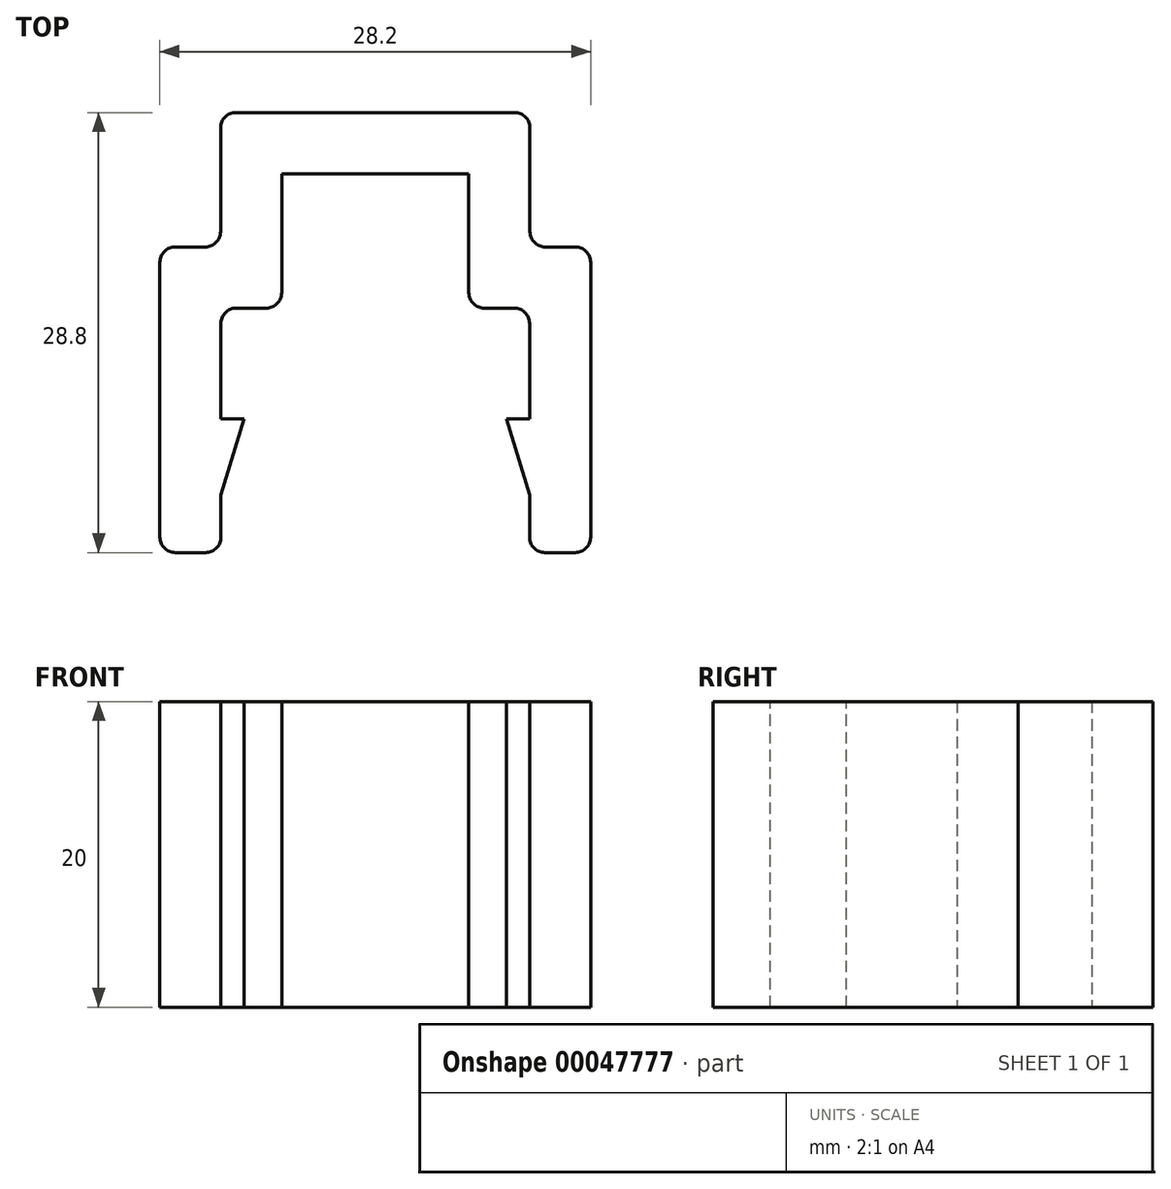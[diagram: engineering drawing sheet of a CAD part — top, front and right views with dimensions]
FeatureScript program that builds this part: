
annotation { "Feature Type Name" : "Feature", "Feature Type Description" : "" }
export const myFeature = defineFeature(function(context is Context, id is Id, definition is map)
    precondition{}
    {
        {
            var Q0;
            Q0=qCreatedBy(makeId("Top.planeOp"),FACE);
            var sketch = newSketch(context, id + "F3", { "sketchPlane" : qUnion([Q0])});
            skLineSegment(sketch, "E0", {"start": v(0, 0) * mm, "end": v(0, 20) * mm});
            skLineSegment(sketch, "E1", {"start": v(0, 20) * mm, "end": v(0, 20) * mm});
            skLineSegment(sketch, "E2", {"start": v(0, 20) * mm, "end": v(3.97, 20) * mm});
            skLineSegment(sketch, "E3", {"start": v(3.97, 20) * mm, "end": v(3.97, 20) * mm});
            skLineSegment(sketch, "E4", {"start": v(3.97, 20) * mm, "end": v(3.97, 28.8) * mm});
            skLineSegment(sketch, "E5", {"start": v(3.97, 28.8) * mm, "end": v(3.97, 28.8) * mm});
            skLineSegment(sketch, "E6", {"start": v(3.97, 28.8) * mm, "end": v(24.23, 28.8) * mm});
            skLineSegment(sketch, "E7", {"start": v(24.23, 28.8) * mm, "end": v(24.23, 20) * mm});
            skLineSegment(sketch, "E8", {"start": v(24.23, 20) * mm, "end": v(28.2, 20) * mm});
            skLineSegment(sketch, "E9", {"start": v(28.2, 20) * mm, "end": v(28.2, 0) * mm});
            skLineSegment(sketch, "E10.0", {"start": v(24.2, 16) * mm, "end": v(24.2, 0) * mm});
            skLineSegment(sketch, "E10.1", {"start": v(20.23, 16) * mm, "end": v(24.2, 16) * mm});
            skLineSegment(sketch, "E10.2", {"start": v(20.23, 24.8) * mm, "end": v(20.23, 16) * mm});
            skLineSegment(sketch, "E10.3", {"start": v(4, 0) * mm, "end": v(4, 16) * mm});
            skLineSegment(sketch, "E10.4", {"start": v(4, 16) * mm, "end": v(7.97, 16) * mm});
            skLineSegment(sketch, "E10.5", {"start": v(7.97, 16) * mm, "end": v(7.97, 24.8) * mm});
            skLineSegment(sketch, "E10.6", {"start": v(7.97, 24.8) * mm, "end": v(20.23, 24.8) * mm});
            skLineSegment(sketch, "E11", {"start": v(0, 0) * mm, "end": v(4, 0) * mm});
            skLineSegment(sketch, "E12", {"start": v(24.2, 0) * mm, "end": v(28.2, 0) * mm});
            skSolve(sketch);
        }
        {
            var Q0;
            Q0 = qSketchRegion(id + "F3", true);
            extrude(context, id + "F0", {"entities" : qUnion([Q0]), "depth" : 20 * mm});
        }
        {
            var Q0;
            Q0=makeQuery(id+"F0.opExtrude","SWEPT_EDGE",EDGE,{"disambiguationData":[OSD([sQuery(id+"F3.wireOp",EDGE,"E10.3"),sQuery(id+"F3.wireOp",EDGE,"E10.4")])]});
            var Q1;
            Q1=makeQuery(id+"F0.opExtrude","SWEPT_EDGE",EDGE,{"disambiguationData":[OSD([sQuery(id+"F3.wireOp",EDGE,"E10.0"),sQuery(id+"F3.wireOp",EDGE,"E10.1")])]});
            var Q2;
            Q2=makeQuery(id+"F0.opExtrude","SWEPT_EDGE",EDGE,{"disambiguationData":[OSD([sQuery(id+"F3.wireOp",EDGE,"E10.4"),sQuery(id+"F3.wireOp",EDGE,"E10.5")])]});
            var Q3;
            Q3=makeQuery(id+"F0.opExtrude","SWEPT_EDGE",EDGE,{"disambiguationData":[OSD([sQuery(id+"F3.wireOp",EDGE,"E10.1"),sQuery(id+"F3.wireOp",EDGE,"E10.2")])]});
            var Q4;
            Q4=makeQuery(id+"F0.opExtrude","SWEPT_EDGE",EDGE,{"disambiguationData":[OSD([sQuery(id+"F3.wireOp",EDGE,"E0"),sQuery(id+"F3.wireOp",EDGE,"E11")])]});
            var Q5;
            Q5=makeQuery(id+"F0.opExtrude","SWEPT_EDGE",EDGE,{"disambiguationData":[OSD([sQuery(id+"F3.wireOp",EDGE,"E10.3"),sQuery(id+"F3.wireOp",EDGE,"E11")])]});
            var Q6;
            Q6=makeQuery(id+"F0.opExtrude","SWEPT_EDGE",EDGE,{"disambiguationData":[OSD([sQuery(id+"F3.wireOp",EDGE,"E10.0"),sQuery(id+"F3.wireOp",EDGE,"E12")])]});
            var Q7;
            Q7=makeQuery(id+"F0.opExtrude","SWEPT_EDGE",EDGE,{"disambiguationData":[OSD([sQuery(id+"F3.wireOp",EDGE,"E9"),sQuery(id+"F3.wireOp",EDGE,"E12")])]});
            var Q8;
            Q8=makeQuery(id+"F0.opExtrude","SWEPT_EDGE",EDGE,{"disambiguationData":[OSD([sQuery(id+"F3.wireOp",EDGE,"E0"),sQuery(id+"F3.wireOp",EDGE,"E2")])]});
            var Q9;
            Q9=makeQuery(id+"F0.opExtrude","SWEPT_EDGE",EDGE,{"disambiguationData":[OSD([sQuery(id+"F3.wireOp",EDGE,"E4"),sQuery(id+"F3.wireOp",EDGE,"E6")])]});
            var Q10;
            Q10=makeQuery(id+"F0.opExtrude","SWEPT_EDGE",EDGE,{"disambiguationData":[OSD([sQuery(id+"F3.wireOp",EDGE,"E2"),sQuery(id+"F3.wireOp",EDGE,"E4")])]});
            var Q11;
            Q11=makeQuery(id+"F0.opExtrude","SWEPT_EDGE",EDGE,{"disambiguationData":[OSD([sQuery(id+"F3.wireOp",EDGE,"E6"),sQuery(id+"F3.wireOp",EDGE,"E7")])]});
            var Q12;
            Q12=makeQuery(id+"F0.opExtrude","SWEPT_EDGE",EDGE,{"disambiguationData":[OSD([sQuery(id+"F3.wireOp",EDGE,"E7"),sQuery(id+"F3.wireOp",EDGE,"E8")])]});
            var Q13;
            Q13=makeQuery(id+"F0.opExtrude","SWEPT_EDGE",EDGE,{"disambiguationData":[OSD([sQuery(id+"F3.wireOp",EDGE,"E8"),sQuery(id+"F3.wireOp",EDGE,"E9")])]});
            fillet(context, id + "F4", {"entities" : qUnion([Q0, Q1, Q2, Q3, Q4, Q5, Q6, Q7, Q8, Q9, Q10, Q11, Q12, Q13]), "radius" : 1 * mm, "tangentPropagation" : true, "allowEdgeOverflow" : false});
        }
        {
            var Q0;
            Q0=makeQuery(id+"F0.opExtrude","CAP_FACE",FACE,{"disambiguationData":[OSD([sQuery(id+"F3.wireOp",EDGE,"E0"),sQuery(id+"F3.wireOp",EDGE,"E2"),sQuery(id+"F3.wireOp",EDGE,"E4"),sQuery(id+"F3.wireOp",EDGE,"E6"),sQuery(id+"F3.wireOp",EDGE,"E7"),sQuery(id+"F3.wireOp",EDGE,"E8"),sQuery(id+"F3.wireOp",EDGE,"E9"),sQuery(id+"F3.wireOp",EDGE,"E10.0"),sQuery(id+"F3.wireOp",EDGE,"E10.1"),sQuery(id+"F3.wireOp",EDGE,"E10.2"),sQuery(id+"F3.wireOp",EDGE,"E10.3"),sQuery(id+"F3.wireOp",EDGE,"E10.4"),sQuery(id+"F3.wireOp",EDGE,"E10.5"),sQuery(id+"F3.wireOp",EDGE,"E10.6"),sQuery(id+"F3.wireOp",EDGE,"E11"),sQuery(id+"F3.wireOp",EDGE,"E12")])],"isStart":false});
            var sketch = newSketch(context, id + "F1", { "sketchPlane" : qUnion([Q0])});
            skLineSegment(sketch, "E13", {"start": v(4, 8.75) * mm, "end": v(5.5, 8.75) * mm});
            skLineSegment(sketch, "E14", {"start": v(5.5, 8.75) * mm, "end": v(4, 3.75) * mm});
            skLineSegment(sketch, "E15", {"start": v(4, 3.75) * mm, "end": v(4, 8.75) * mm});
            skLineSegment(sketch, "E16", {"start": v(14.1, 24.8) * mm, "end": v(14.1, 0) * mm, "construction": true});
            skLineSegment(sketch, "E17.MirrorCS", {"start": v(22.7, 8.75) * mm, "end": v(24.2, 3.75) * mm});
            skLineSegment(sketch, "E18.MirrorCS", {"start": v(24.2, 3.75) * mm, "end": v(24.2, 8.75) * mm});
            skLineSegment(sketch, "E19.MirrorCS", {"start": v(24.2, 8.75) * mm, "end": v(22.7, 8.75) * mm});
            skSolve(sketch);
        }
        {
            var Q0;
            Q0=makeQuery(id+"F1.imprint","IMPRINT",FACE,{"disambiguationData":[TD([[makeQuery(id+"F1.imprint","IMPRINT",EDGE,{"derivedFrom":sQuery(id+"F1.wireOp",EDGE,"E13")}),-1.0]])]});
            var Q1;
            Q1=makeQuery(id+"F1.imprint","IMPRINT",FACE,{"disambiguationData":[TD([[makeQuery(id+"F1.imprint","IMPRINT",EDGE,{"derivedFrom":sQuery(id+"F1.wireOp",EDGE,"E17.MirrorCS")}),1.0]])]});
            extrude(context, id + "F2", {"entities" : qUnion([Q0, Q1]), "operationType" : NewBodyOperationType.ADD, "oppositeDirection" : true, "depth" : 20 * mm});
        }
    });
